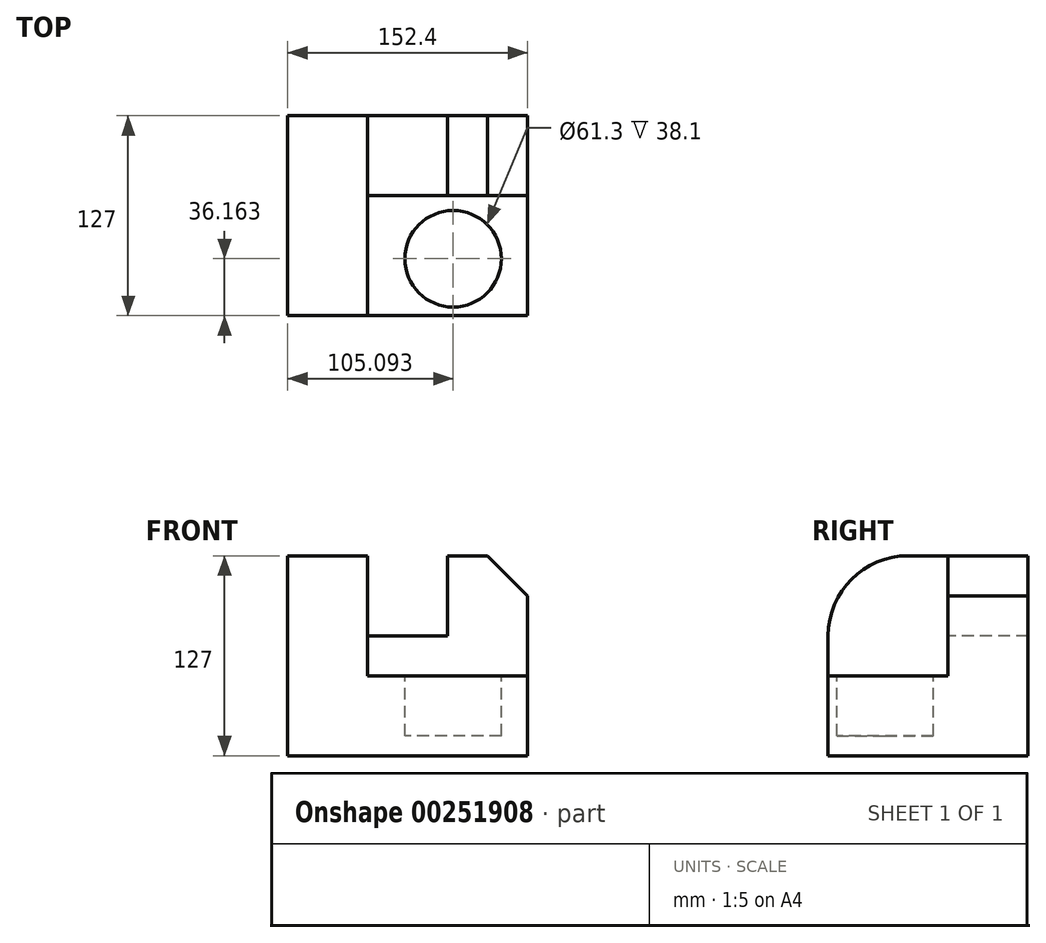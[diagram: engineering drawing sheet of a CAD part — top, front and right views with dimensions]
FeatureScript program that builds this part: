
annotation { "Feature Type Name" : "Feature", "Feature Type Description" : "" }
export const myFeature = defineFeature(function(context is Context, id is Id, definition is map)
    precondition{}
    {
        {
            var Q0;
            Q0=qCreatedBy(makeId("Top.planeOp"),FACE);
            var sketch = newSketch(context, id + "F0", { "sketchPlane" : qUnion([Q0])});
            skLineSegment(sketch, "E0.bottom", {"start": v(-76.2, 63.5) * mm, "end": v(76.2, 63.5) * mm});
            skLineSegment(sketch, "E0.top", {"start": v(-76.2, -63.5) * mm, "end": v(76.2, -63.5) * mm});
            skLineSegment(sketch, "E0.left", {"start": v(-76.2, 63.5) * mm, "end": v(-76.2, -63.5) * mm});
            skLineSegment(sketch, "E0.right", {"start": v(76.2, 63.5) * mm, "end": v(76.2, -63.5) * mm});
            skPoint(sketch, "E0.middle", {"position": v(0, 0) * mm});
            skSolve(sketch);
        }
        {
            var Q0;
            Q0 = qSketchRegion(id + "F0", true);
            extrude(context, id + "F1", {"entities" : qUnion([Q0]), "endBound" : BoundingType.SYMMETRIC, "depth" : 127 * mm});
        }
        {
            var Q0;
            Q0=makeQuery(id+"F1.opExtrude","CAP_FACE",FACE,{"disambiguationData":[OSD([sQuery(id+"F0.wireOp",EDGE,"E0.bottom"),sQuery(id+"F0.wireOp",EDGE,"E0.top"),sQuery(id+"F0.wireOp",EDGE,"E0.left"),sQuery(id+"F0.wireOp",EDGE,"E0.right")])],"isStart":false});
            var sketch = newSketch(context, id + "F2", { "sketchPlane" : qUnion([Q0])});
            skLineSegment(sketch, "E1", {"start": v(76.2, -63.5) * mm, "end": v(76.2, 12.7) * mm});
            skLineSegment(sketch, "E2", {"start": v(76.2, -63.5) * mm, "end": v(-25.4, -63.5) * mm});
            skLineSegment(sketch, "E3", {"start": v(-25.4, -63.5) * mm, "end": v(-25.4, 12.7) * mm});
            skLineSegment(sketch, "E4", {"start": v(-25.4, 12.7) * mm, "end": v(76.2, 12.7) * mm});
            skSolve(sketch);
        }
        {
            var Q0;
            Q0=makeQuery(id+"F2.imprint","IMPRINT",FACE,{"disambiguationData":[TD([[makeQuery(id+"F2.imprint","IMPRINT",EDGE,{"derivedFrom":sQuery(id+"F2.wireOp",EDGE,"E1")}),-1.0]])]});
            extrude(context, id + "F3", {"entities" : qUnion([Q0]), "operationType" : NewBodyOperationType.REMOVE, "oppositeDirection" : true, "depth" : 76.2 * mm});
        }
        {
            var Q0;
            Q0=makeQuery(id+"F1.opExtrude","CAP_EDGE",EDGE,{"disambiguationData":[OSD([sQuery(id+"F0.wireOp",EDGE,"E0.top")])],"isStart":false});
            fillet(context, id + "F4", {"entities" : qUnion([Q0]), "radius" : 50.8 * mm, "tangentPropagation" : true, "allowEdgeOverflow" : false});
        }
        {
            var Q0;
            Q0=makeQuery(id+"F3.boolean.opBoolean","COPY",FACE,{"derivedFrom":makeQuery(id+"F3.opExtrude","CAP_FACE",FACE,{"disambiguationData":[OSD([sQuery(id+"F2.wireOp",EDGE,"E1"),sQuery(id+"F2.wireOp",EDGE,"E2"),sQuery(id+"F2.wireOp",EDGE,"E3"),sQuery(id+"F2.wireOp",EDGE,"E4")])],"isStart":false})});
            var sketch = newSketch(context, id + "F5", { "sketchPlane" : qUnion([Q0])});
            skCircle(sketch, "E5", {"center": v(28.9, -27.34) * mm, "radius": 30.65 * mm});
            skSolve(sketch);
        }
        {
            var Q0;
            Q0=makeQuery(id+"F5.imprint","IMPRINT",FACE,{"disambiguationData":[TD([[makeQuery(id+"F5.imprint","IMPRINT",EDGE,{"derivedFrom":sQuery(id+"F5.wireOp",EDGE,"E5")}),1.0]])]});
            extrude(context, id + "F6", {"entities" : qUnion([Q0]), "operationType" : NewBodyOperationType.REMOVE, "oppositeDirection" : true, "depth" : 38.1 * mm});
        }
        {
            var Q0;
            Q0=makeQuery(id+"F1.opExtrude","CAP_FACE",FACE,{"disambiguationData":[OSD([sQuery(id+"F0.wireOp",EDGE,"E0.bottom"),sQuery(id+"F0.wireOp",EDGE,"E0.top"),sQuery(id+"F0.wireOp",EDGE,"E0.left"),sQuery(id+"F0.wireOp",EDGE,"E0.right")])],"isStart":false});
            var sketch = newSketch(context, id + "F7", { "sketchPlane" : qUnion([Q0])});
            skLineSegment(sketch, "E6", {"start": v(-25.4, 12.7) * mm, "end": v(25.4, 12.7) * mm});
            skLineSegment(sketch, "E7", {"start": v(25.4, 12.7) * mm, "end": v(25.4, 63.5) * mm});
            skLineSegment(sketch, "E8", {"start": v(25.4, 63.5) * mm, "end": v(-25.4, 63.5) * mm});
            skLineSegment(sketch, "E9", {"start": v(-25.4, 63.5) * mm, "end": v(-25.4, 12.7) * mm});
            skSolve(sketch);
        }
        {
            var Q0;
            Q0=makeQuery(id+"F7.imprint","IMPRINT",FACE,{"disambiguationData":[TD([[makeQuery(id+"F7.imprint","IMPRINT",EDGE,{"derivedFrom":sQuery(id+"F7.wireOp",EDGE,"E6")}),1.0]])]});
            extrude(context, id + "F8", {"entities" : qUnion([Q0]), "operationType" : NewBodyOperationType.REMOVE, "oppositeDirection" : true, "depth" : 50.8 * mm});
        }
        {
            var Q0;
            Q0=makeQuery(id+"F1.opExtrude","CAP_EDGE",EDGE,{"disambiguationData":[OSD([sQuery(id+"F0.wireOp",EDGE,"E0.right")])],"isStart":false});
            chamfer(context, id + "F9", {"entities" : qUnion([Q0]), "width" : 25.4 * mm, "tangentPropagation" : true});
        }
    });
